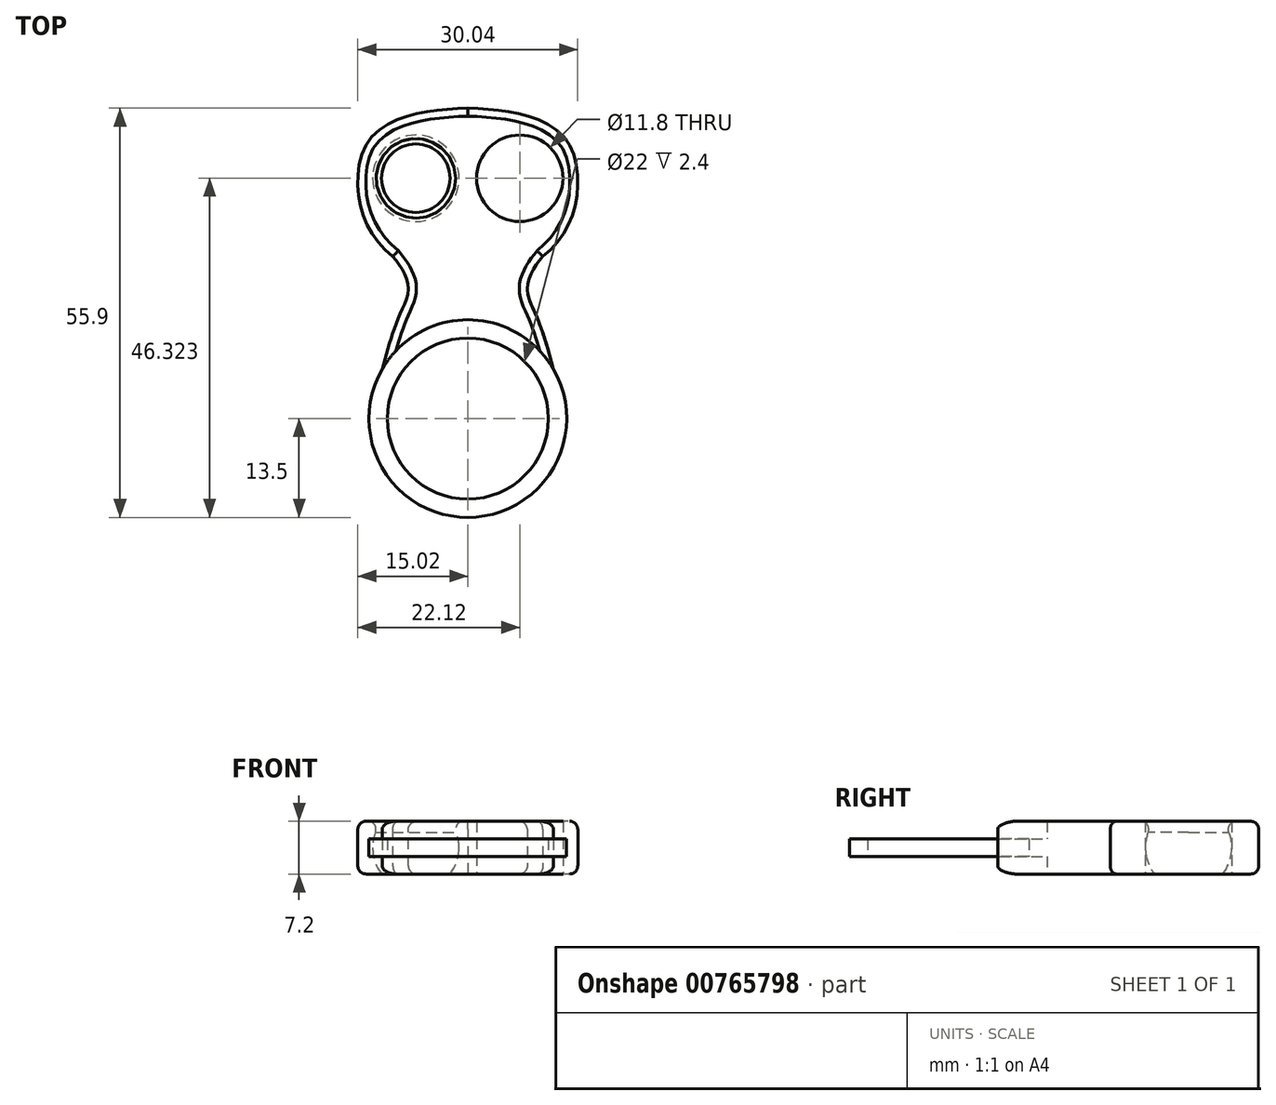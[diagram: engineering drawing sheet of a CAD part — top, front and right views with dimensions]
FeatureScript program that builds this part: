
annotation { "Feature Type Name" : "Feature", "Feature Type Description" : "" }
export const myFeature = defineFeature(function(context is Context, id is Id, definition is map)
    precondition{}
    {
        {
            var Q0;
            Q0=qCreatedBy(makeId("Top.planeOp"),FACE);
            var sketch = newSketch(context, id + "F0", { "sketchPlane" : qUnion([Q0])});
            skCircle(sketch, "E0", {"center": v(0, 0) * mm, "radius": 11 * mm});
            skCircle(sketch, "E1", {"center": v(0, 0) * mm, "radius": 13.5 * mm});
            skLineSegment(sketch, "E2", {"start": v(-60.62, 35) * mm, "end": v(57.4, -33.14) * mm, "construction": true});
            skLineSegment(sketch, "E3.MirrorCS", {"start": v(-60.62, -35) * mm, "end": v(57.4, 33.14) * mm, "construction": true});
            skFitSpline(sketch, "E4", {"points": [v(-11.7, 6.75) * mm, v(-8.5, 16) * mm, v(-10.25, 22.14) * mm], "startDerivative": vector(9.34, 35.35) * mm, "endDerivative": vector(-17.9, 20.96) * mm});
            skLineSegment(sketch, "E5", {"start": v(-61.07, 42.4) * mm, "end": v(58.93, 42.4) * mm, "construction": true});
            skFitSpline(sketch, "E6", {"points": [v(-10.25, 22.14) * mm, v(-14.98, 33.35) * mm, v(0, 42.4) * mm], "startDerivative": vector(-26.2, 21.36) * mm, "endDerivative": vector(68.91, 1.84) * mm});
            skCircle(sketch, "E7", {"center": v(-7.1, 32.82) * mm, "radius": 5.9 * mm});
            skFitSpline(sketch, "E8.MirrorCS", {"points": [v(10.25, 22.14) * mm, v(14.98, 33.35) * mm, v(0, 42.4) * mm], "startDerivative": vector(26.2, 21.36) * mm, "endDerivative": vector(-68.91, 1.84) * mm});
            skFitSpline(sketch, "E9.MirrorCS", {"points": [v(11.7, 6.75) * mm, v(8.5, 16) * mm, v(10.25, 22.14) * mm], "startDerivative": vector(-9.34, 35.35) * mm, "endDerivative": vector(17.9, 20.96) * mm});
            skCircle(sketch, "E10.MirrorC", {"center": v(7.1, 32.82) * mm, "radius": 5.9 * mm});
            skSolve(sketch);
        }
        {
            var Q0;
            {var subQ0=sQuery(id+"F0.wireOp",EDGE,"E4");Q0=makeQuery(id+"F0.imprint","IMPRINT",FACE,{"disambiguationData":[TD([[makeQuery(id+"F0.imprint","IMPRINT",EDGE,{"derivedFrom":subQ0}),-1.0]])]});}
            var Q1;
            Q1=makeQuery(id+"F0.imprint","IMPRINT",FACE,{"disambiguationData":[TD([[makeQuery(id+"F0.imprint","IMPRINT",EDGE,{"derivedFrom":sQuery(id+"F0.wireOp",EDGE,"E7")}),1.0]])]});
            var Q2;
            Q2=makeQuery(id+"F0.imprint","IMPRINT",FACE,{"disambiguationData":[TD([[makeQuery(id+"F0.imprint","IMPRINT",EDGE,{"derivedFrom":sQuery(id+"F0.wireOp",EDGE,"E10.MirrorC")}),-1.0]])]});
            extrude(context, id + "F1", {"entities" : qUnion([Q0, Q1, Q2]), "depth" : 7.2 * mm, "offsetDistance" : 25 * mm});
        }
        {
            var Q0;
            Q0=qCreatedBy(makeId("Top.planeOp"),FACE);
            cPlane(context, id + "F2", {"entities" : qUnion([Q0]), "cplaneType" : CPlaneType.OFFSET, "offset" : 3.6 * mm, "width" : 150 * mm, "height" : 150 * mm});
        }
        {
            var Q0;
            Q0=qCreatedBy(id+"F2.planeOp",FACE);
            var sketch = newSketch(context, id + "F3", { "sketchPlane" : qUnion([Q0])});
            skArc(sketch, "E11.0", {"start": v(-1.2, 32.82) * mm, "mid": v(-7.1, 38.72) * mm, "end": v(-13, 32.82) * mm});
            skArc(sketch, "E12.0", {"start": v(1.2, 32.82) * mm, "mid": v(7.1, 38.72) * mm, "end": v(13, 32.82) * mm});
            skLineSegment(sketch, "E13", {"start": v(-13, 32.82) * mm, "end": v(-1.2, 32.82) * mm});
            skLineSegment(sketch, "E14.MirrorCS", {"start": v(13, 32.82) * mm, "end": v(1.2, 32.82) * mm});
            skSolve(sketch);
        }
        {
            var Q0;
            Q0=qSketchRegion(id+"F3",true);
            var Q1;
            Q1=sQuery(id+"F3.wireOp",EDGE,"E14.MirrorCS");
            revolve(context, id + "F4", {"operationType" : NewBodyOperationType.REMOVE, "surfaceOperationType" : NewSurfaceOperationType.NEW, "entities" : qUnion([Q0]), "axis" : qUnion([Q1]), "revolveType" : RevolveType.FULL, "oppositeDirection" : true});
        }
        {
            var Q0;
            Q0=makeQuery(id+"F4.boolean.opBoolean","INTERSECT",EDGE,{"derivedFrom":[makeQuery(id+"F1.opExtrude","CAP_FACE",FACE,{"disambiguationData":[OSD([sQuery(id+"F0.wireOp",EDGE,"E1"),sQuery(id+"F0.wireOp",EDGE,"E4"),sQuery(id+"F0.wireOp",EDGE,"E6"),sQuery(id+"F0.wireOp",EDGE,"E8.MirrorCS"),sQuery(id+"F0.wireOp",EDGE,"E9.MirrorCS")])],"isStart":false}),makeQuery(id+"F4.opRevolve","SWEPT_FACE",FACE,{"disambiguationData":[OSD([sQuery(id+"F3.wireOp",EDGE,"E11.0")])]})]});
            var Q1;
            Q1=makeQuery(id+"F4.boolean.opBoolean","INTERSECT",EDGE,{"derivedFrom":[makeQuery(id+"F1.opExtrude","CAP_FACE",FACE,{"disambiguationData":[OSD([sQuery(id+"F0.wireOp",EDGE,"E1"),sQuery(id+"F0.wireOp",EDGE,"E4"),sQuery(id+"F0.wireOp",EDGE,"E6"),sQuery(id+"F0.wireOp",EDGE,"E8.MirrorCS"),sQuery(id+"F0.wireOp",EDGE,"E9.MirrorCS")])],"isStart":false}),makeQuery(id+"F4.opRevolve","SWEPT_FACE",FACE,{"disambiguationData":[OSD([sQuery(id+"F3.wireOp",EDGE,"E12.0")])]})]});
            fillet(context, id + "F5", {"entities" : qUnion([Q0, Q1]), "radius" : 1.1 * mm, "tangentPropagation" : true, "allowEdgeOverflow" : false});
        }
        {
            var Q0;
            Q0=makeQuery(id+"F1.opExtrude","CAP_EDGE",EDGE,{"disambiguationData":[OSD([sQuery(id+"F0.wireOp",EDGE,"E6")])],"isStart":false});
            var Q1;
            Q1=makeQuery(id+"F1.opExtrude","CAP_EDGE",EDGE,{"disambiguationData":[OSD([sQuery(id+"F0.wireOp",EDGE,"E4")])],"isStart":false});
            var Q2;
            Q2=makeQuery(id+"F1.opExtrude","CAP_EDGE",EDGE,{"disambiguationData":[OSD([sQuery(id+"F0.wireOp",EDGE,"E8.MirrorCS")])],"isStart":false});
            var Q3;
            Q3=makeQuery(id+"F1.opExtrude","CAP_EDGE",EDGE,{"disambiguationData":[OSD([sQuery(id+"F0.wireOp",EDGE,"E9.MirrorCS")])],"isStart":false});
            var Q4;
            Q4=makeQuery(id+"FGJ5H7MxzaZfUph_1.opExtrude","CAP_EDGE",EDGE,{"disambiguationData":[OSD([sQuery(id+"F0.wireOp",EDGE,"E1")])],"isStart":true});
            var Q5;
            Q5=makeQuery(id+"F1.opExtrude","CAP_EDGE",EDGE,{"disambiguationData":[OSD([sQuery(id+"F0.wireOp",EDGE,"E4")])],"isStart":true});
            var Q6;
            Q6=makeQuery(id+"F1.opExtrude","CAP_EDGE",EDGE,{"disambiguationData":[OSD([sQuery(id+"F0.wireOp",EDGE,"E9.MirrorCS")])],"isStart":true});
            var Q7;
            Q7=makeQuery(id+"F1.opExtrude","CAP_EDGE",EDGE,{"disambiguationData":[OSD([sQuery(id+"F0.wireOp",EDGE,"E8.MirrorCS")])],"isStart":true});
            var Q8;
            Q8=makeQuery(id+"F1.opExtrude","CAP_EDGE",EDGE,{"disambiguationData":[OSD([sQuery(id+"F0.wireOp",EDGE,"E6")])],"isStart":true});
            fillet(context, id + "F6", {"entities" : qUnion([Q0, Q1, Q2, Q3, Q4, Q5, Q6, Q7, Q8]), "radius" : 1.1 * mm, "tangentPropagation" : true, "allowEdgeOverflow" : false});
        }
        {
            var Q0;
            Q0=qCreatedBy(makeId("Top.planeOp"),FACE);
            cPlane(context, id + "F7", {"entities" : qUnion([Q0]), "cplaneType" : CPlaneType.OFFSET, "offset" : 2.4 * mm, "width" : 150 * mm, "height" : 150 * mm});
        }
        {
            var Q0;
            Q0=qCreatedBy(id+"F7.planeOp",FACE);
            var sketch = newSketch(context, id + "F8", { "sketchPlane" : qUnion([Q0])});
            skCircle(sketch, "E15.0", {"center": v(0, 0) * mm, "radius": 13.5 * mm});
            skCircle(sketch, "E15.1", {"center": v(0, 0) * mm, "radius": 11 * mm});
            skSolve(sketch);
        }
        {
            var Q0;
            Q0=makeQuery(id+"F8.imprint","IMPRINT",FACE,{"disambiguationData":[TD([[makeQuery(id+"F8.imprint","IMPRINT",EDGE,{"derivedFrom":sQuery(id+"F8.wireOp",EDGE,"E15.0")}),1.0]])]});
            extrude(context, id + "F9", {"entities" : qUnion([Q0]), "operationType" : NewBodyOperationType.ADD, "depth" : 2.4 * mm, "offsetDistance" : 25 * mm});
        }
    });
